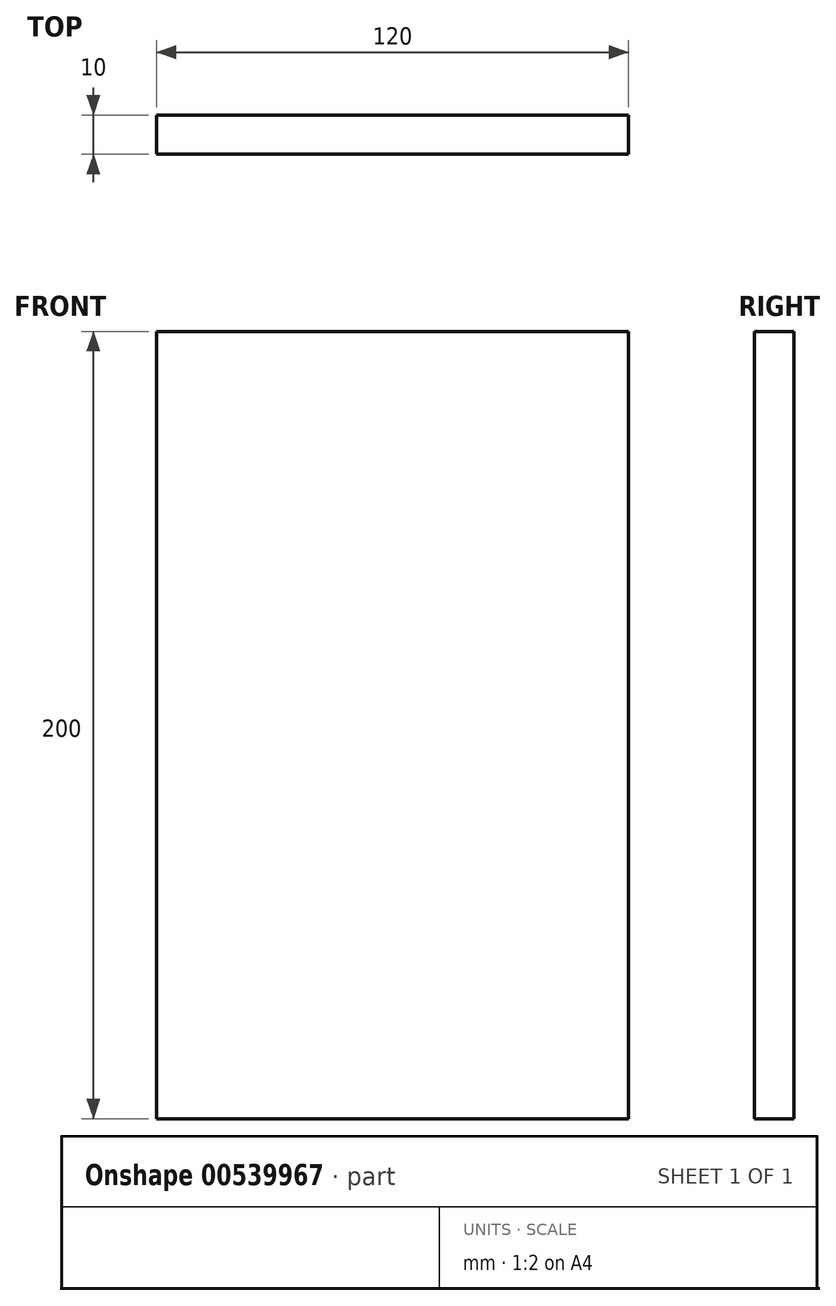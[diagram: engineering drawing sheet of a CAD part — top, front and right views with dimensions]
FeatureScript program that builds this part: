
annotation { "Feature Type Name" : "Feature", "Feature Type Description" : "" }
export const myFeature = defineFeature(function(context is Context, id is Id, definition is map)
    precondition{}
    {
        {
            var Q0;
            Q0=qCreatedBy(makeId("Front.planeOp"),FACE);
            var sketch = newSketch(context, id + "F0", { "sketchPlane" : qUnion([Q0])});
            skLineSegment(sketch, "E0.bottom", {"start": v(-67.95, 100) * mm, "end": v(52.05, 100) * mm});
            skLineSegment(sketch, "E0.top", {"start": v(-67.95, -100) * mm, "end": v(52.05, -100) * mm});
            skLineSegment(sketch, "E0.left", {"start": v(-67.95, 100) * mm, "end": v(-67.95, -100) * mm});
            skLineSegment(sketch, "E0.right", {"start": v(52.05, 100) * mm, "end": v(52.05, -100) * mm});
            skPoint(sketch, "E0.middle", {"position": v(-7.95, 0) * mm});
            skSolve(sketch);
        }
        {
            var Q0;
            Q0=makeQuery(id+"F0.imprint","IMPRINT",FACE,{"disambiguationData":[TD([[makeQuery(id+"F0.imprint","IMPRINT",EDGE,{"derivedFrom":sQuery(id+"F0.wireOp",EDGE,"E0.bottom")}),-1.0]])]});
            extrude(context, id + "F1", {"entities" : qUnion([Q0]), "depth" : 10 * mm, "offsetDistance" : 25 * mm});
        }
    });
